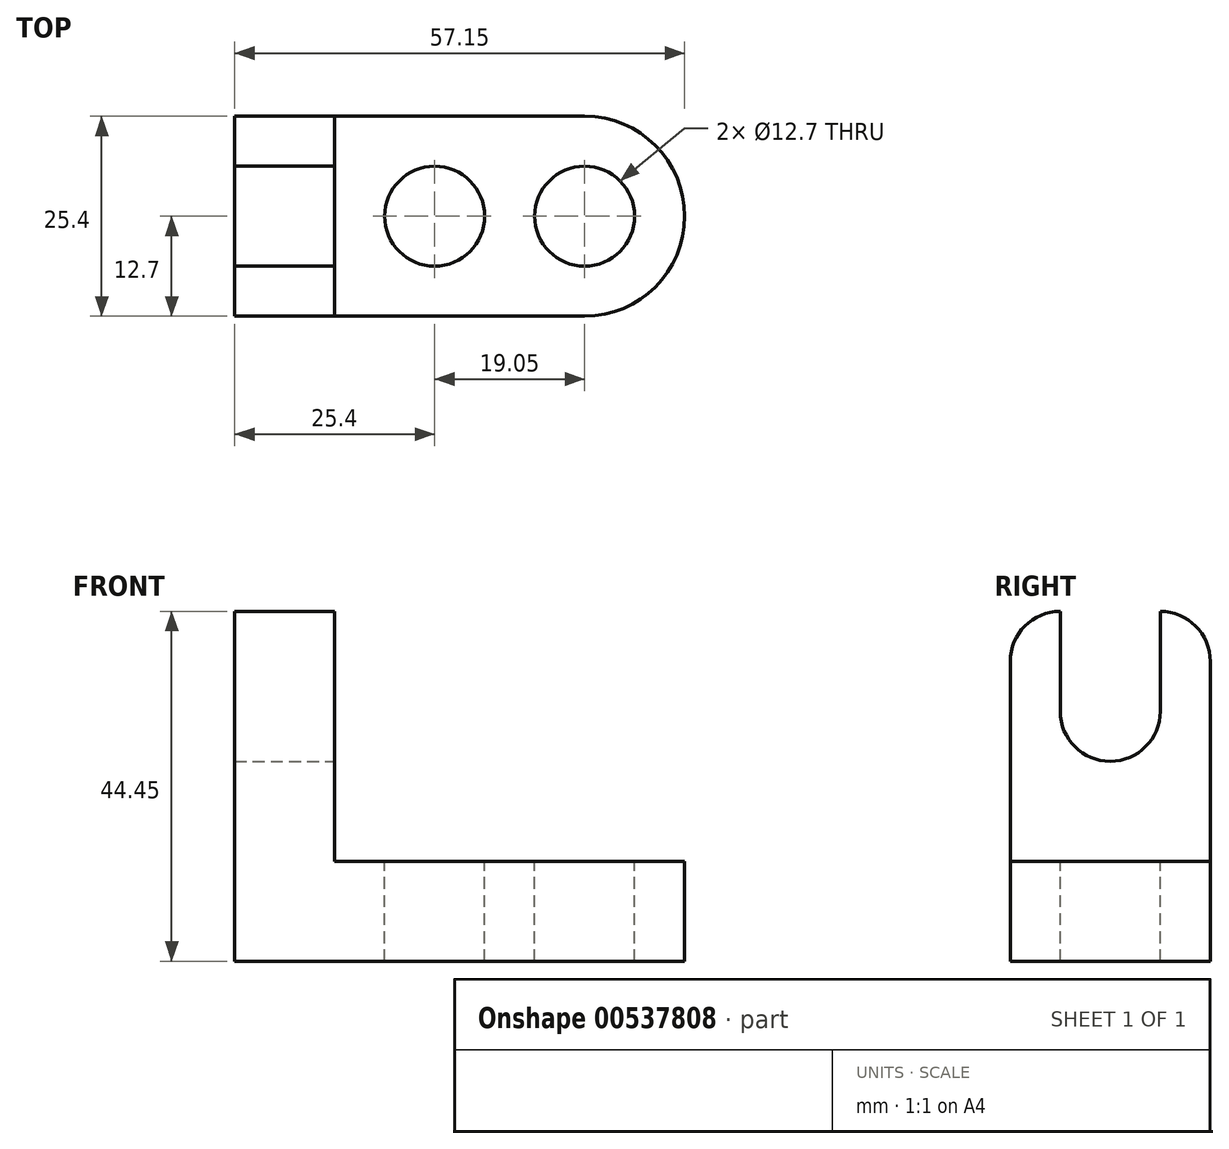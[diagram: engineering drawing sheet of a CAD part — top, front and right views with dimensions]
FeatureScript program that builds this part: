
annotation { "Feature Type Name" : "Feature", "Feature Type Description" : "" }
export const myFeature = defineFeature(function(context is Context, id is Id, definition is map)
    precondition{}
    {
        {
            var Q0;
            Q0=qCreatedBy(makeId("Front.planeOp"),FACE);
            var sketch = newSketch(context, id + "F0", { "sketchPlane" : qUnion([Q0])});
            skLineSegment(sketch, "E0", {"start": v(0, 0) * mm, "end": v(57.15, 0) * mm});
            skLineSegment(sketch, "E1", {"start": v(57.15, 0) * mm, "end": v(57.15, 12.7) * mm});
            skLineSegment(sketch, "E2", {"start": v(57.15, 12.7) * mm, "end": v(12.7, 12.7) * mm});
            skLineSegment(sketch, "E3", {"start": v(12.7, 12.7) * mm, "end": v(12.7, 44.45) * mm});
            skLineSegment(sketch, "E4", {"start": v(12.7, 44.45) * mm, "end": v(0, 44.45) * mm});
            skLineSegment(sketch, "E5", {"start": v(0, 44.45) * mm, "end": v(0, 0) * mm});
            skSolve(sketch);
        }
        {
            var Q0;
            Q0=makeQuery(id+"F0.imprint","IMPRINT",FACE,{"disambiguationData":[TD([[makeQuery(id+"F0.imprint","IMPRINT",EDGE,{"derivedFrom":sQuery(id+"F0.wireOp",EDGE,"E0")}),1.0]])]});
            extrude(context, id + "F1", {"entities" : qUnion([Q0]), "depth" : 25.4 * mm, "offsetDistance" : 25.4 * mm});
        }
        {
            var Q0;
            Q0=makeQuery(id+"F1.opExtrude","SWEPT_FACE",FACE,{"disambiguationData":[OSD([sQuery(id+"F0.wireOp",EDGE,"E2")])]});
            var sketch = newSketch(context, id + "F2", { "sketchPlane" : qUnion([Q0])});
            skCircle(sketch, "E6", {"center": v(25.4, -12.7) * mm, "radius": 6.35 * mm});
            skCircle(sketch, "E7", {"center": v(44.45, -12.7) * mm, "radius": 6.35 * mm});
            skPoint(sketch, "E8.orphan", {"position": v(44.45, 0) * mm});
            skPoint(sketch, "E9.orphan", {"position": v(44.45, -25.4) * mm});
            skArc(sketch, "E10", {"start": v(44.45, -25.4) * mm, "mid": v(57.15, -12.7) * mm, "end": v(44.45, 0) * mm});
            skSolve(sketch);
        }
        {
            var Q0;
            Q0=makeQuery(id+"F2.imprint","IMPRINT",FACE,{"disambiguationData":[TD([[makeQuery(id+"F2.imprint","IMPRINT",EDGE,{"derivedFrom":sQuery(id+"F2.wireOp",EDGE,"E7")}),1.0]])]});
            var Q1;
            Q1=makeQuery(id+"F2.imprint","IMPRINT",FACE,{"disambiguationData":[TD([[makeQuery(id+"F2.imprint","IMPRINT",EDGE,{"derivedFrom":sQuery(id+"F2.wireOp",EDGE,"E6")}),1.0]])]});
            var Q2;
            {var subQ0=sQuery(id+"F2.wireOp",EDGE,"E10");var subQ1=sQuery(id+"F0.wireOp",EDGE,"E2");var subQ2=makeQuery(id+"F1.opExtrude","CAP_EDGE",EDGE,{"disambiguationData":[OSD([subQ1])],"isStart":true});var subQ3=makeQuery(id+"F2.imprint","INTERSECT",VERTEX,{"derivedFrom":[subQ2,subQ0]});Q2=makeQuery(id+"F2.imprint","IMPRINT",FACE,{"disambiguationData":[TD([[makeQuery(id+"F2.imprint","IMPRINT",EDGE,{"disambiguationData":[TD([[subQ3,1.0]])],"derivedFrom":subQ0}),-1.0]])]});}
            var Q3;
            {var subQ0=sQuery(id+"F2.wireOp",EDGE,"E10");var subQ1=sQuery(id+"F0.wireOp",EDGE,"E2");var subQ2=makeQuery(id+"F1.opExtrude","CAP_EDGE",EDGE,{"disambiguationData":[OSD([subQ1])],"isStart":false});var subQ3=makeQuery(id+"F2.imprint","INTERSECT",VERTEX,{"derivedFrom":[subQ2,subQ0]});Q3=makeQuery(id+"F2.imprint","IMPRINT",FACE,{"disambiguationData":[TD([[makeQuery(id+"F2.imprint","IMPRINT",EDGE,{"disambiguationData":[TD([[subQ3,-1.0]])],"derivedFrom":subQ0}),-1.0]])]});}
            extrude(context, id + "F3", {"entities" : qUnion([Q0, Q1, Q2, Q3]), "operationType" : NewBodyOperationType.REMOVE, "oppositeDirection" : true, "depth" : 25.4 * mm, "offsetDistance" : 25.4 * mm});
        }
        {
            var Q0;
            Q0=makeQuery(id+"F1.opExtrude","SWEPT_FACE",FACE,{"disambiguationData":[OSD([sQuery(id+"F0.wireOp",EDGE,"E3")])]});
            var sketch = newSketch(context, id + "F4", { "sketchPlane" : qUnion([Q0])});
            skCircle(sketch, "E11", {"center": v(-12.7, 31.75) * mm, "radius": 6.35 * mm});
            skLineSegment(sketch, "E12", {"start": v(-19.05, 31.75) * mm, "end": v(-19.05, 44.45) * mm});
            skLineSegment(sketch, "E13", {"start": v(-6.35, 31.75) * mm, "end": v(-6.35, 44.45) * mm});
            skPoint(sketch, "E14.endSnap0", {"position": v(-19.05, 38.1) * mm});
            skPoint(sketch, "E14.end.orphan", {"position": v(-25.4, 38.1) * mm});
            skPoint(sketch, "E15.end.orphan", {"position": v(-6.35, 44.45) * mm});
            skPoint(sketch, "E15.start.orphan", {"position": v(0, 38.1) * mm});
            skArc(sketch, "E16", {"start": v(-19.05, 44.45) * mm, "mid": v(-23.54, 42.6) * mm, "end": v(-25.4, 38.1) * mm});
            skPoint(sketch, "E17.center.orphan", {"position": v(2.13, 46.58) * mm});
            skPoint(sketch, "E18.start.orphan", {"position": v(-6.35, 38.1) * mm});
            skArc(sketch, "E19", {"start": v(0, 38.1) * mm, "mid": v(-1.86, 42.6) * mm, "end": v(-6.35, 44.45) * mm});
            skSolve(sketch);
        }
        {
            var Q0;
            {var subQ0=sQuery(id+"F4.wireOp",EDGE,"E19");Q0=makeQuery(id+"F4.imprint","IMPRINT",FACE,{"disambiguationData":[TD([[makeQuery(id+"F4.imprint","IMPRINT",EDGE,{"derivedFrom":subQ0}),-1.0]])]});}
            var Q1;
            {var subQ0=sQuery(id+"F4.wireOp",EDGE,"E12");Q1=makeQuery(id+"F4.imprint","IMPRINT",FACE,{"disambiguationData":[TD([[makeQuery(id+"F4.imprint","IMPRINT",EDGE,{"derivedFrom":subQ0}),-1.0]])]});}
            var Q2;
            {var subQ0=sQuery(id+"F4.wireOp",EDGE,"E11");var subQ1=makeQuery(id+"F4.imprint","INTERSECT",VERTEX,{"derivedFrom":[subQ0,sQuery(id+"F4.wireOp",EDGE,"E12")]});Q2=makeQuery(id+"F4.imprint","IMPRINT",FACE,{"disambiguationData":[TD([[makeQuery(id+"F4.imprint","IMPRINT",EDGE,{"disambiguationData":[TD([[subQ1,1.0]])],"derivedFrom":subQ0}),1.0]])]});}
            var Q3;
            {var subQ0=sQuery(id+"F4.wireOp",EDGE,"E16");Q3=makeQuery(id+"F4.imprint","IMPRINT",FACE,{"disambiguationData":[TD([[makeQuery(id+"F4.imprint","IMPRINT",EDGE,{"derivedFrom":subQ0}),-1.0]])]});}
            extrude(context, id + "F5", {"entities" : qUnion([Q0, Q1, Q2, Q3]), "operationType" : NewBodyOperationType.REMOVE, "oppositeDirection" : true, "depth" : 25.4 * mm, "offsetDistance" : 25.4 * mm});
        }
    });
